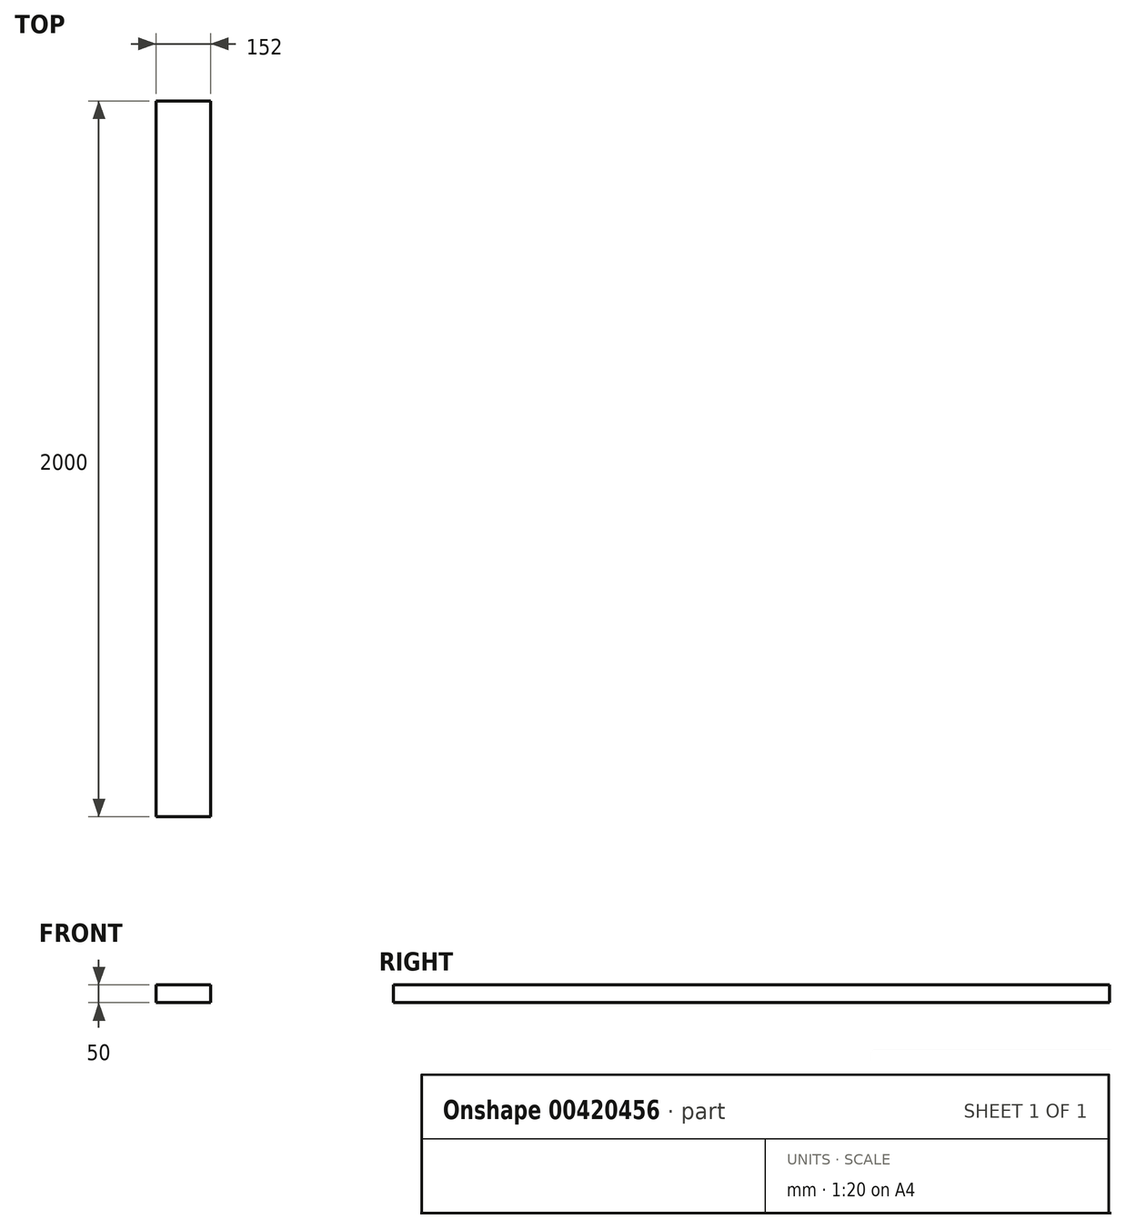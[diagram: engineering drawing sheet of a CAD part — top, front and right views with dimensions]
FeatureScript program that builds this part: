
annotation { "Feature Type Name" : "Feature", "Feature Type Description" : "" }
export const myFeature = defineFeature(function(context is Context, id is Id, definition is map)
    precondition{}
    {
        {
            var Q0;
            Q0=qCreatedBy(makeId("Front.planeOp"),FACE);
            var sketch = newSketch(context, id + "F0", { "sketchPlane" : qUnion([Q0])});
            skLineSegment(sketch, "E0.bottom", {"start": v(76, 25) * mm, "end": v(-76, 25) * mm});
            skLineSegment(sketch, "E0.top", {"start": v(76, -25) * mm, "end": v(-76, -25) * mm});
            skLineSegment(sketch, "E0.left", {"start": v(76, 25) * mm, "end": v(76, -25) * mm});
            skLineSegment(sketch, "E0.right", {"start": v(-76, 25) * mm, "end": v(-76, -25) * mm});
            skPoint(sketch, "E0.middle", {"position": v(0, 0) * mm});
            skSolve(sketch);
        }
        {
            var Q0;
            Q0=makeQuery(id+"F0.imprint","IMPRINT",FACE,{"disambiguationData":[TD([[makeQuery(id+"F0.imprint","IMPRINT",EDGE,{"derivedFrom":sQuery(id+"F0.wireOp",EDGE,"E0.bottom")}),1.0]])]});
            extrude(context, id + "F1", {"entities" : qUnion([Q0]), "endBound" : BoundingType.SYMMETRIC, "depth" : 2000 * mm});
        }
    });
